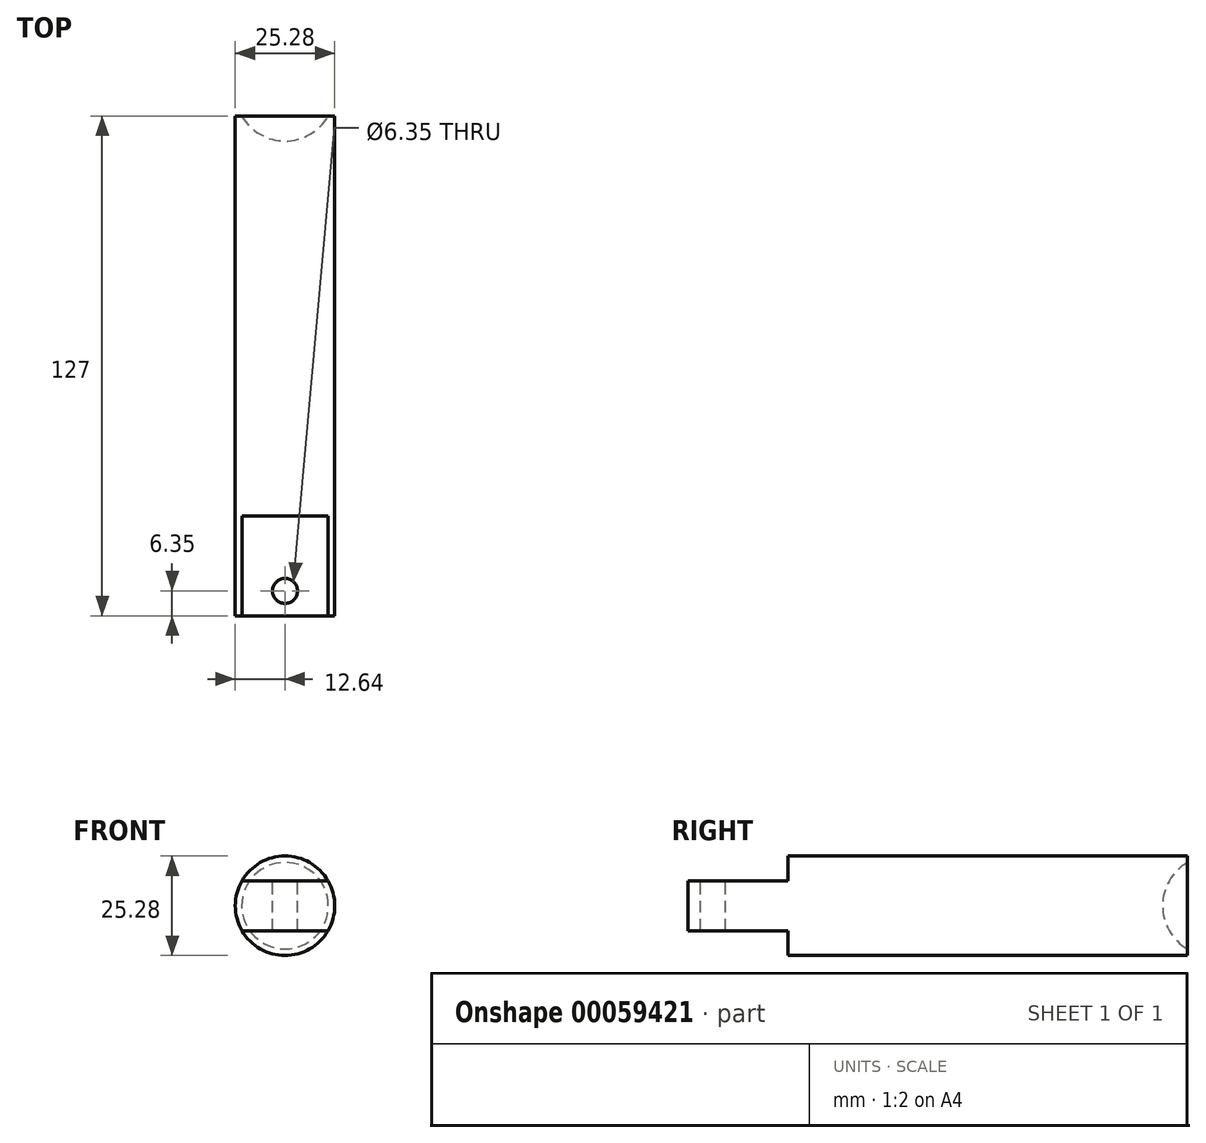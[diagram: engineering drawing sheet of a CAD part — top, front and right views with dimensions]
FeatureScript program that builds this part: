
annotation { "Feature Type Name" : "Feature", "Feature Type Description" : "" }
export const myFeature = defineFeature(function(context is Context, id is Id, definition is map)
    precondition{}
    {
        {
            var Q0;
            Q0=qCreatedBy(makeId("Front.planeOp"),FACE);
            var sketch = newSketch(context, id + "F0", { "sketchPlane" : qUnion([Q0])});
            skCircle(sketch, "E0", {"center": v(0, 0) * mm, "radius": 12.64 * mm});
            skSolve(sketch);
        }
        {
            var Q0;
            Q0 = qSketchRegion(id + "F0", true);
            extrude(context, id + "F1", {"entities" : qUnion([Q0]), "depth" : 127 * mm});
        }
        {
            var Q0;
            Q0=makeQuery(id+"F1.opExtrude","CAP_FACE",FACE,{"disambiguationData":[OSD([sQuery(id+"F0.wireOp",EDGE,"E0")])],"isStart":false});
            var sketch = newSketch(context, id + "F2", { "sketchPlane" : qUnion([Q0])});
            skLineSegment(sketch, "E1.bottom", {"start": v(-20.18, 19.66) * mm, "end": v(24.87, 19.66) * mm});
            skLineSegment(sketch, "E1.top", {"start": v(-20.18, 6.35) * mm, "end": v(24.87, 6.35) * mm});
            skLineSegment(sketch, "E1.left", {"start": v(-20.18, 19.66) * mm, "end": v(-20.18, 6.35) * mm});
            skLineSegment(sketch, "E1.right", {"start": v(24.87, 19.66) * mm, "end": v(24.87, 6.35) * mm});
            skLineSegment(sketch, "E2.bottom", {"start": v(-21.77, -6.35) * mm, "end": v(29.03, -6.35) * mm});
            skLineSegment(sketch, "E2.top", {"start": v(-21.77, -15.27) * mm, "end": v(29.03, -15.27) * mm});
            skLineSegment(sketch, "E2.left", {"start": v(-21.77, -6.35) * mm, "end": v(-21.77, -15.27) * mm});
            skLineSegment(sketch, "E2.right", {"start": v(29.03, -6.35) * mm, "end": v(29.03, -15.27) * mm});
            skLineSegment(sketch, "E3", {"start": v(-23.77, 0) * mm, "end": v(26.06, 0) * mm, "construction": true});
            skSolve(sketch);
        }
        {
            var Q0;
            Q0 = qSketchRegion(id + "F2", true);
            extrude(context, id + "F3", {"entities" : qUnion([Q0]), "operationType" : NewBodyOperationType.REMOVE, "oppositeDirection" : true, "depth" : 25.4 * mm});
        }
        {
            var Q0;
            Q0=qCreatedBy(makeId("Front.planeOp"),FACE);
            cPlane(context, id + "F4", {"entities" : qUnion([Q0]), "cplaneType" : CPlaneType.OFFSET, "offset" : 6.35 * mm, "oppositeDirection" : true, "width" : 152.4 * mm, "height" : 152.4 * mm});
        }
        {
            var Q0;
            Q0=qCreatedBy(id+"F4.planeOp",FACE);
            var sketch = newSketch(context, id + "F5", { "sketchPlane" : qUnion([Q0])});
            skArc(sketch, "E4", {"start": v(12.7, 0) * mm, "mid": v(0, 12.7) * mm, "end": v(-12.7, 0) * mm});
            skLineSegment(sketch, "E5", {"start": v(34.69, 0) * mm, "end": v(-31.69, 0) * mm, "construction": true});
            skLineSegment(sketch, "E6", {"start": v(12.7, 0) * mm, "end": v(-12.7, 0) * mm});
            skSolve(sketch);
        }
        {
            var Q0;
            Q0 = qSketchRegion(id + "F5", true);
            var Q1;
            Q1=sQuery(id+"F5.wireOp",EDGE,"E5");
            revolve(context, id + "F6", {"operationType" : NewBodyOperationType.REMOVE, "entities" : qUnion([Q0]), "axis" : qUnion([Q1]), "revolveType" : RevolveType.FULL, "oppositeDirection" : true});
        }
        {
            var Q0;
            Q0=makeQuery(id+"F3.boolean.opBoolean","COPY",FACE,{"derivedFrom":makeQuery(id+"F3.opExtrude","SWEPT_FACE",FACE,{"disambiguationData":[OSD([sQuery(id+"F2.wireOp",EDGE,"E1.top")])]})});
            var sketch = newSketch(context, id + "F7", { "sketchPlane" : qUnion([Q0])});
            skCircle(sketch, "E7", {"center": v(0, -120.65) * mm, "radius": 3.18 * mm});
            skSolve(sketch);
        }
        {
            var Q0;
            Q0 = qSketchRegion(id + "F7", true);
            extrude(context, id + "F8", {"entities" : qUnion([Q0]), "operationType" : NewBodyOperationType.REMOVE, "oppositeDirection" : true, "depth" : 25.4 * mm});
        }
    });
